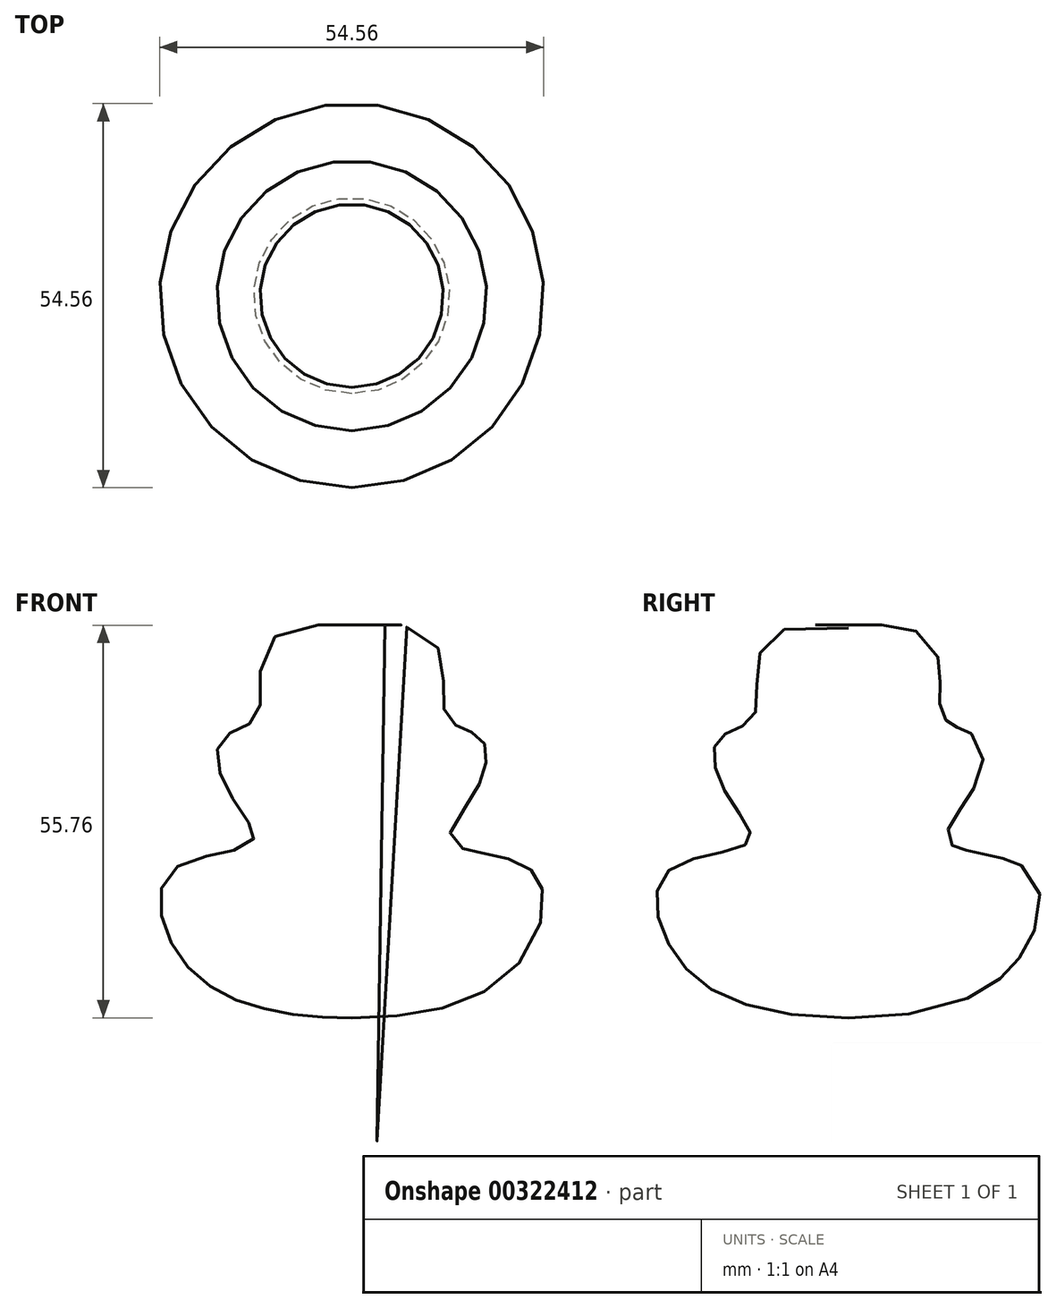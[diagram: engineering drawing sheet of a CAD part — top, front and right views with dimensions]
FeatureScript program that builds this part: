
annotation { "Feature Type Name" : "Feature", "Feature Type Description" : "" }
export const myFeature = defineFeature(function(context is Context, id is Id, definition is map)
    precondition{}
    {
        {
            var Q0;
            Q0=qCreatedBy(makeId("Right.planeOp"),FACE);
            var sketch = newSketch(context, id + "F0", { "sketchPlane" : qUnion([Q0])});
            skFitSpline(sketch, "E0", {"points": [v(0, 0) * mm, v(-25.46, 10.3) * mm, v(-25.32, 21.13) * mm, v(-14.12, 25.02) * mm, v(-17.7, 32.42) * mm, v(-18.27, 39.78) * mm, v(-13.18, 43.4) * mm, v(0, 55.37) * mm], "startDerivative": vector(-208.48, 0) * mm, "endDerivative": vector(295.74, -44.28) * mm});
            skLineSegment(sketch, "E1", {"start": v(0, 55.37) * mm, "end": v(0, 0) * mm});
            skSolve(sketch);
        }
        {
            var Q0;
            {var subQ0=sQuery(id+"F0.wireOp",EDGE,"E1");var subQ1=sQuery(id+"F0.wireOp",EDGE,"E0");var subQ2=makeQuery(id+"F0.imprint","INTERSECT",VERTEX,{"disambiguationData":[OD(0.0)],"derivedFrom":[subQ1,subQ0]});Q0=makeQuery(id+"F0.imprint","IMPRINT",FACE,{"disambiguationData":[TD([[makeQuery(id+"F0.imprint","IMPRINT",EDGE,{"disambiguationData":[TD([[subQ2,-1.0]])],"derivedFrom":subQ1}),-1.0]])]});}
            var Q1;
            Q1=sQuery(id+"F0.wireOp",EDGE,"E1");
            revolve(context, id + "F1", {"entities" : qUnion([Q0]), "axis" : qUnion([Q1]), "revolveType" : RevolveType.FULL});
        }
    });
